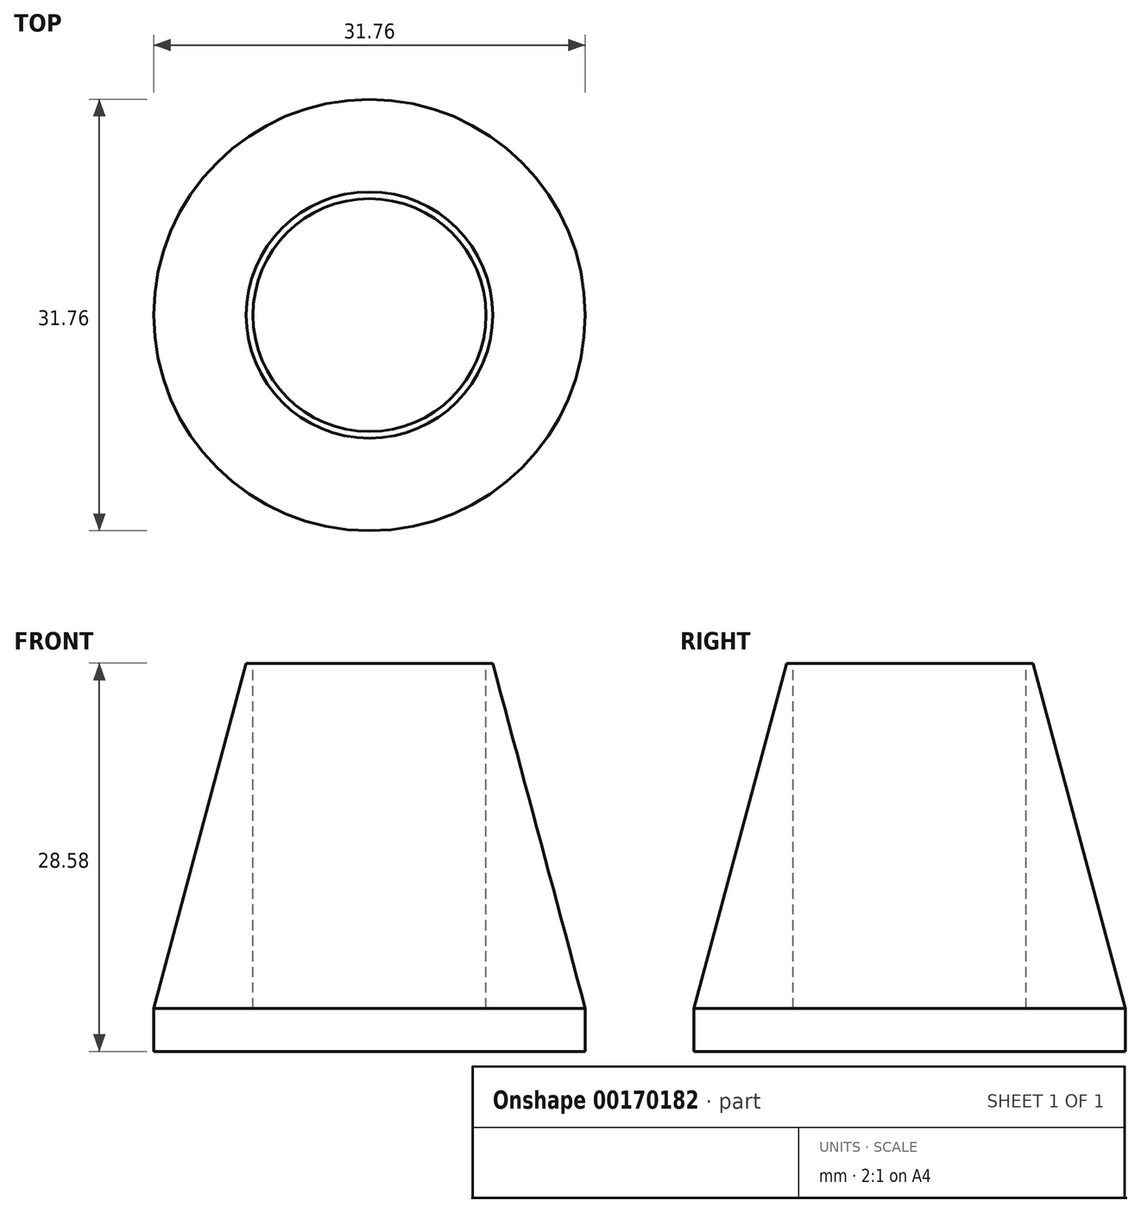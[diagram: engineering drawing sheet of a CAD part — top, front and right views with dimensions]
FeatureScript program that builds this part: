
annotation { "Feature Type Name" : "Feature", "Feature Type Description" : "" }
export const myFeature = defineFeature(function(context is Context, id is Id, definition is map)
    precondition{}
    {
        {
            var Q0;
            Q0=qCreatedBy(makeId("Top.planeOp"),FACE);
            var sketch = newSketch(context, id + "F0", { "sketchPlane" : qUnion([Q0])});
            skCircle(sketch, "E0", {"center": v(0, 0) * mm, "radius": 15.88 * mm});
            skSolve(sketch);
        }
        {
            var Q0;
            Q0=makeQuery(id+"F0.imprint","IMPRINT",FACE,{"disambiguationData":[TD([[makeQuery(id+"F0.imprint","IMPRINT",EDGE,{"derivedFrom":sQuery(id+"F0.wireOp",EDGE,"E0")}),1.0]])]});
            extrude(context, id + "F1", {"entities" : qUnion([Q0]), "depth" : 3.17 * mm});
        }
        {
            var Q0;
            Q0=makeQuery(id+"F1.opExtrude","CAP_FACE",FACE,{"disambiguationData":[OSD([sQuery(id+"F0.wireOp",EDGE,"E0")])],"isStart":false});
            extrude(context, id + "F2", {"entities" : qUnion([Q0]), "operationType" : NewBodyOperationType.ADD, "depth" : 25.4 * mm, "hasDraft" : true, "draftAngle" : 15 * degree, "draftPullDirection" : true});
        }
        {
            var Q0;
            Q0=makeQuery(id+"F2.opExtrude","CAP_FACE",FACE,{"disambiguationData":[OSD([sQuery(id+"F0.wireOp",EDGE,"E0")])],"isStart":false});
            var sketch = newSketch(context, id + "F3", { "sketchPlane" : qUnion([Q0])});
            skCircle(sketch, "E1", {"center": v(0, 0) * mm, "radius": 8.57 * mm});
            skSolve(sketch);
        }
        {
            var Q0;
            Q0=makeQuery(id+"F3.imprint","IMPRINT",FACE,{"disambiguationData":[TD([[makeQuery(id+"F3.imprint","IMPRINT",EDGE,{"derivedFrom":sQuery(id+"F3.wireOp",EDGE,"E1")}),1.0]])]});
            extrude(context, id + "F4", {"entities" : qUnion([Q0]), "operationType" : NewBodyOperationType.REMOVE, "oppositeDirection" : true, "depth" : 25.4 * mm});
        }
    });
